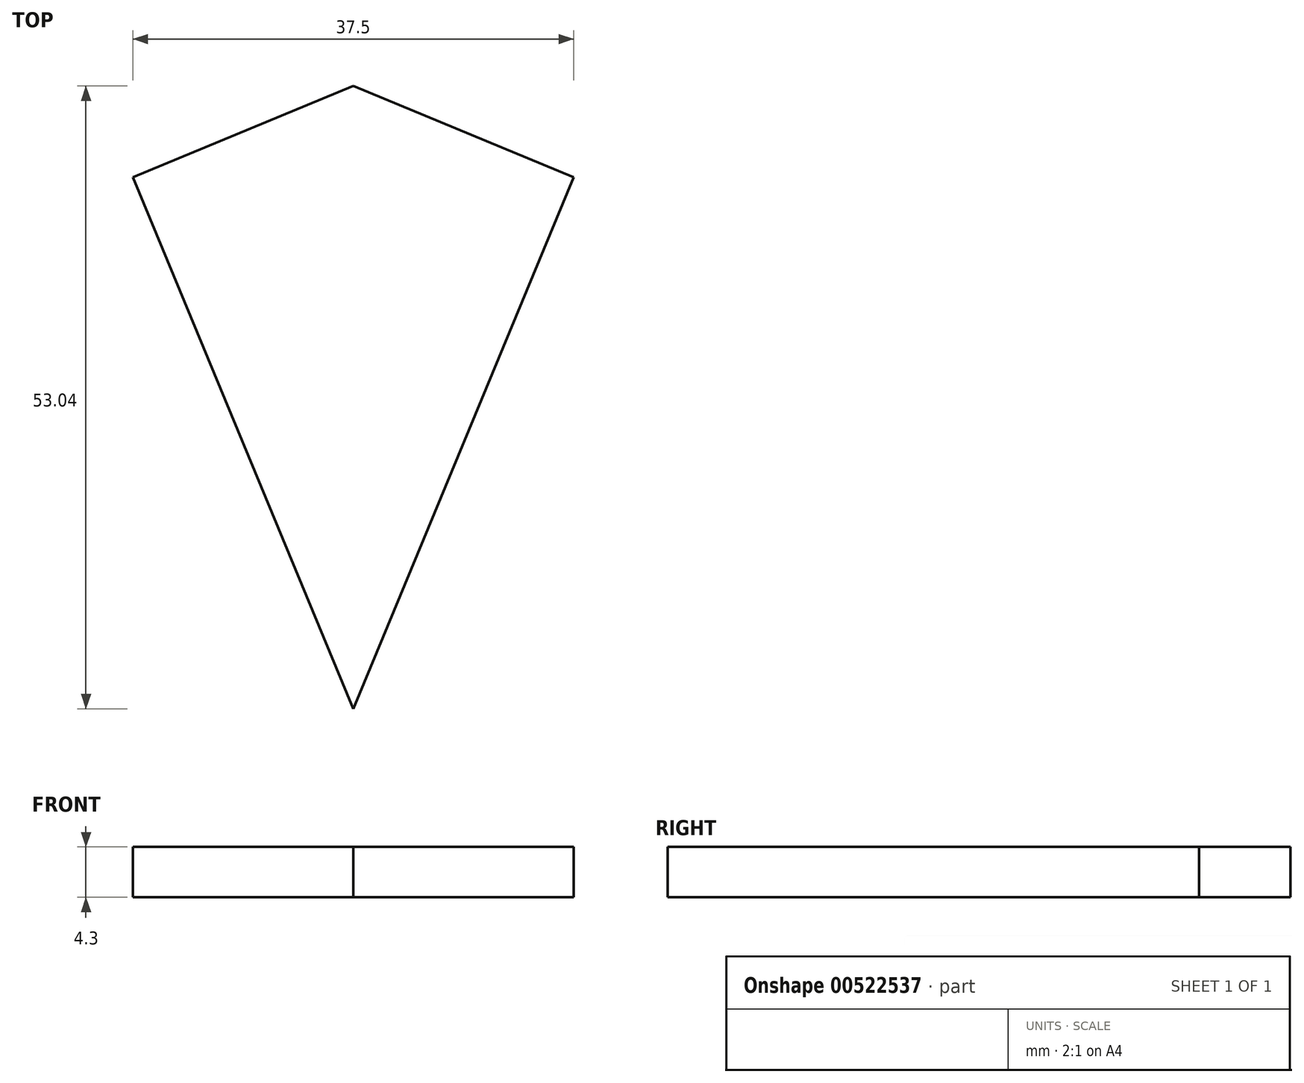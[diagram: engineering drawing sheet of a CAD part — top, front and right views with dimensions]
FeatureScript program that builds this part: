
annotation { "Feature Type Name" : "Feature", "Feature Type Description" : "" }
export const myFeature = defineFeature(function(context is Context, id is Id, definition is map)
    precondition{}
    {
        {
            var Q0;
            Q0=qCreatedBy(makeId("Top.planeOp"),FACE);
            var sketch = newSketch(context, id + "F0", { "sketchPlane" : qUnion([Q0])});
            skLineSegment(sketch, "E0", {"start": v(0, -45.27) * mm, "end": v(18.75, 0) * mm});
            skLineSegment(sketch, "E1", {"start": v(18.75, 0) * mm, "end": v(0, 7.77) * mm});
            skLineSegment(sketch, "E2", {"start": v(0, 7.77) * mm, "end": v(-18.75, 0) * mm});
            skLineSegment(sketch, "E3", {"start": v(-18.75, 0) * mm, "end": v(0, -45.27) * mm});
            skSolve(sketch);
        }
        {
            var Q0;
            Q0 = qSketchRegion(id + "F0", true);
            extrude(context, id + "F1", {"entities" : qUnion([Q0]), "depth" : 4.3 * mm, "offsetDistance" : 25 * mm});
        }
    });
